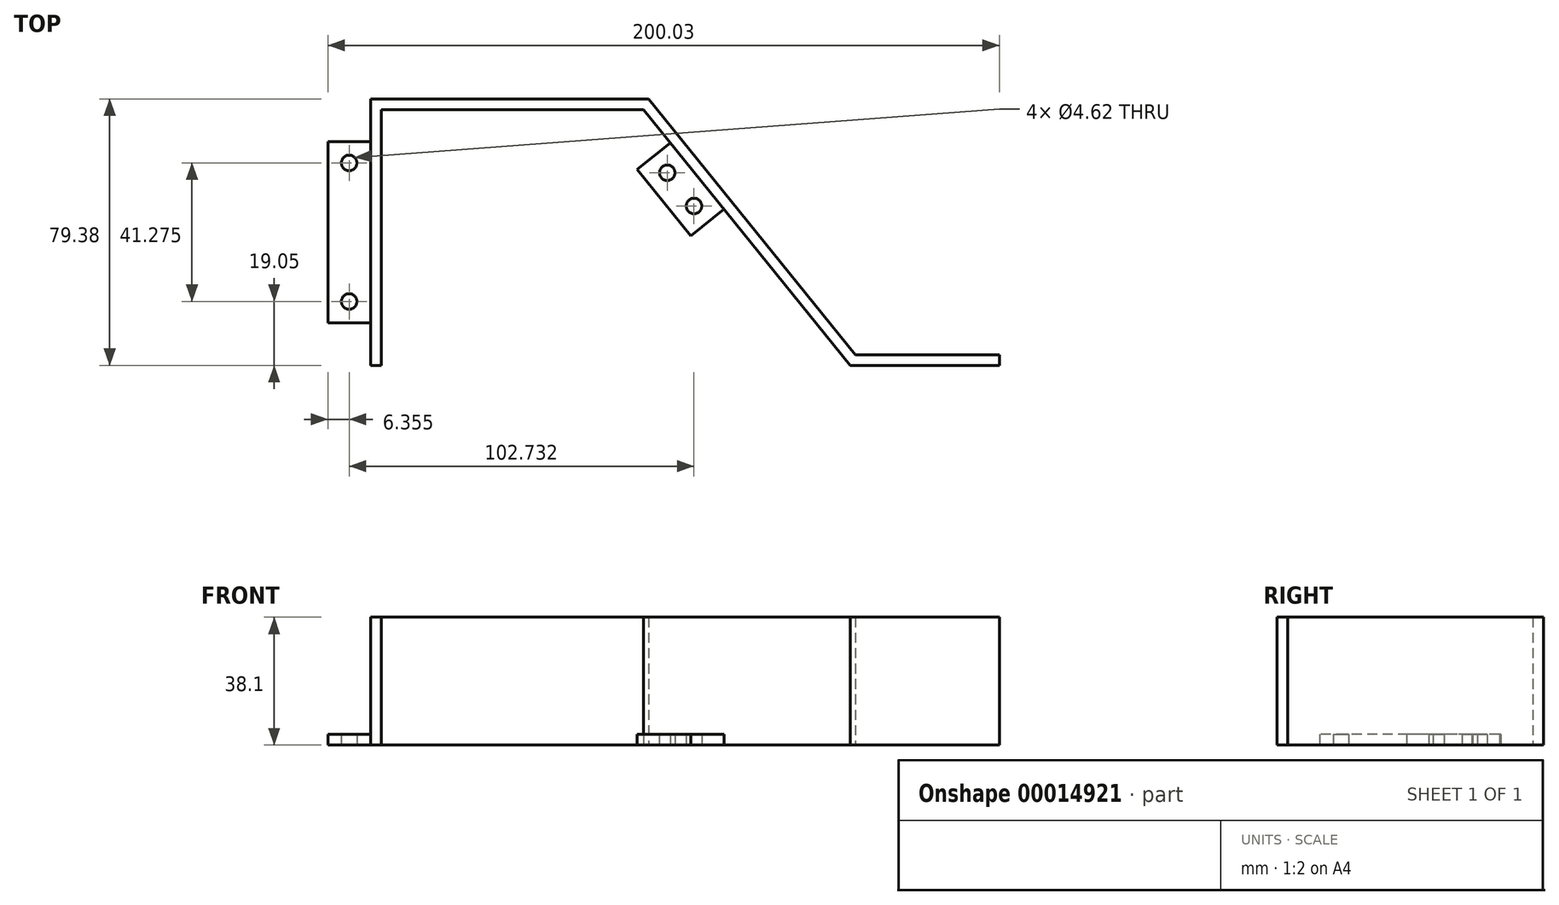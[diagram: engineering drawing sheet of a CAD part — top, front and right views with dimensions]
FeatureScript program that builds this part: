
annotation { "Feature Type Name" : "Feature", "Feature Type Description" : "" }
export const myFeature = defineFeature(function(context is Context, id is Id, definition is map)
    precondition{}
    {
        {
            var Q0;
            Q0=qCreatedBy(makeId("Top.planeOp"),FACE);
            var sketch = newSketch(context, id + "F0", { "sketchPlane" : qUnion([Q0])});
            skLineSegment(sketch, "E0", {"start": v(0, 0) * mm, "end": v(50.8, 0) * mm});
            skLineSegment(sketch, "E1", {"start": v(139.7, -76.2) * mm, "end": v(184.15, -76.2) * mm});
            skLineSegment(sketch, "E2", {"start": v(50.8, 0) * mm, "end": v(79.73, 0) * mm});
            skLineSegment(sketch, "E3", {"start": v(79.73, 0) * mm, "end": v(79.73, -24.8) * mm});
            skLineSegment(sketch, "E4", {"start": v(0, 0) * mm, "end": v(0, -76.2) * mm});
            skLineSegment(sketch, "E5.bottom", {"start": v(0, 0) * mm, "end": v(79.73, 0) * mm});
            skLineSegment(sketch, "E5.top", {"start": v(0, 3.18) * mm, "end": v(79.73, 3.18) * mm});
            skLineSegment(sketch, "E5.left", {"start": v(0, 0) * mm, "end": v(0, 3.18) * mm});
            skLineSegment(sketch, "E5.right", {"start": v(79.73, 0) * mm, "end": v(79.73, 3.17) * mm});
            skLineSegment(sketch, "E6.bottom", {"start": v(0, 3.18) * mm, "end": v(-3.18, 3.18) * mm});
            skLineSegment(sketch, "E6.top", {"start": v(0, -76.2) * mm, "end": v(-3.17, -76.2) * mm});
            skLineSegment(sketch, "E6.left", {"start": v(0, 3.18) * mm, "end": v(0, -76.2) * mm});
            skLineSegment(sketch, "E6.right", {"start": v(-3.18, 3.18) * mm, "end": v(-3.17, -76.2) * mm});
            skLineSegment(sketch, "E7.top", {"start": v(139.7, -73.02) * mm, "end": v(184.15, -73.02) * mm});
            skLineSegment(sketch, "E7.left", {"start": v(139.7, -76.2) * mm, "end": v(139.7, -73.02) * mm});
            skLineSegment(sketch, "E7.right", {"start": v(184.15, -76.2) * mm, "end": v(184.15, -73.02) * mm});
            skLineSegment(sketch, "E8", {"start": v(79.73, 0) * mm, "end": v(139.7, -76.2) * mm});
            skLineSegment(sketch, "E9.bottom", {"start": v(77.26, 1.18) * mm, "end": v(139.7, -76.2) * mm});
            skLineSegment(sketch, "E9.top", {"start": v(79.73, 3.18) * mm, "end": v(142.17, -74.2) * mm});
            skLineSegment(sketch, "E9.left", {"start": v(77.26, 1.18) * mm, "end": v(79.73, 3.17) * mm});
            skLineSegment(sketch, "E9.right", {"start": v(139.7, -76.2) * mm, "end": v(142.17, -74.2) * mm});
            skLineSegment(sketch, "E10", {"start": v(139.7, -76.2) * mm, "end": v(50.8, 0) * mm});
            skSolve(sketch);
        }
        {
            var Q0;
            {var subQ3=sQuery(id+"F0.wireOp",EDGE,"E6.bottom");Q0=makeQuery(id+"F0.imprint","IMPRINT",FACE,{"disambiguationData":[TD([[makeQuery(id+"F0.imprint","IMPRINT",EDGE,{"derivedFrom":subQ3}),1.0]])]});}
            var Q1;
            {var subQ5=sQuery(id+"F0.wireOp",EDGE,"E5.top");Q1=makeQuery(id+"F0.imprint","IMPRINT",FACE,{"disambiguationData":[TD([[makeQuery(id+"F0.imprint","IMPRINT",EDGE,{"derivedFrom":subQ5}),-1.0]])]});}
            var Q2;
            {var subQ4=sQuery(id+"F0.wireOp",EDGE,"E5.right");Q2=makeQuery(id+"F0.imprint","IMPRINT",FACE,{"disambiguationData":[TD([[makeQuery(id+"F0.imprint","IMPRINT",EDGE,{"derivedFrom":subQ4}),1.0]])]});}
            var Q3;
            {var subQ0=sQuery(id+"F0.wireOp",EDGE,"E9.bottom");var subQ3=sQuery(id+"F0.wireOp",EDGE,"E3");var subQ4=makeQuery(id+"F0.imprint","INTERSECT",VERTEX,{"derivedFrom":[subQ3,subQ0]});Q3=makeQuery(id+"F0.imprint","IMPRINT",FACE,{"disambiguationData":[TD([[makeQuery(id+"F0.imprint","IMPRINT",EDGE,{"disambiguationData":[TD([[subQ4,1.0]])],"derivedFrom":subQ0}),1.0]])]});}
            var Q4;
            {var subQ3=sQuery(id+"F0.wireOp",EDGE,"E8");Q4=makeQuery(id+"F0.imprint","IMPRINT",FACE,{"disambiguationData":[TD([[makeQuery(id+"F0.imprint","IMPRINT",EDGE,{"derivedFrom":subQ3}),-1.0]])]});}
            var Q5;
            {var subQ3=sQuery(id+"F0.wireOp",EDGE,"E5.right");Q5=makeQuery(id+"F0.imprint","IMPRINT",FACE,{"disambiguationData":[TD([[makeQuery(id+"F0.imprint","IMPRINT",EDGE,{"derivedFrom":subQ3}),-1.0]])]});}
            var Q6;
            {var subQ4=sQuery(id+"F0.wireOp",EDGE,"E7.left");Q6=makeQuery(id+"F0.imprint","IMPRINT",FACE,{"disambiguationData":[TD([[makeQuery(id+"F0.imprint","IMPRINT",EDGE,{"derivedFrom":subQ4}),-1.0]])]});}
            var Q7;
            Q7=makeQuery(id+"F0.imprint","IMPRINT",FACE,{"disambiguationData":[TD([[makeQuery(id+"F0.imprint","IMPRINT",EDGE,{"derivedFrom":sQuery(id+"F0.wireOp",EDGE,"E1")}),1.0]])]});
            extrude(context, id + "F1", {"entities" : qUnion([Q0, Q1, Q2, Q3, Q4, Q5, Q6, Q7]), "depth" : 38.1 * mm});
        }
        {
            var Q0;
            Q0=qCreatedBy(makeId("Top.planeOp"),FACE);
            var sketch = newSketch(context, id + "F2", { "sketchPlane" : qUnion([Q0])});
            skLineSegment(sketch, "E11.bottom", {"start": v(86.19, -9.88) * mm, "end": v(76.3, -17.86) * mm});
            skLineSegment(sketch, "E11.top", {"start": v(102.14, -29.65) * mm, "end": v(92.25, -37.63) * mm});
            skLineSegment(sketch, "E11.left", {"start": v(86.19, -9.88) * mm, "end": v(102.14, -29.65) * mm});
            skLineSegment(sketch, "E11.right", {"start": v(76.3, -17.86) * mm, "end": v(92.25, -37.63) * mm});
            skCircle(sketch, "E12", {"center": v(85.23, -18.81) * mm, "radius": 2.31 * mm});
            skCircle(sketch, "E13", {"center": v(93.2, -28.7) * mm, "radius": 2.31 * mm});
            skLineSegment(sketch, "E14.bottom", {"start": v(-15.88, -9.52) * mm, "end": v(-3.18, -9.52) * mm});
            skLineSegment(sketch, "E14.top", {"start": v(-15.88, -63.5) * mm, "end": v(-3.18, -63.5) * mm});
            skLineSegment(sketch, "E14.left", {"start": v(-15.88, -9.52) * mm, "end": v(-15.88, -63.5) * mm});
            skLineSegment(sketch, "E14.right", {"start": v(-3.18, -9.52) * mm, "end": v(-3.18, -63.5) * mm});
            skCircle(sketch, "E15", {"center": v(-9.53, -57.15) * mm, "radius": 2.31 * mm});
            skCircle(sketch, "E16", {"center": v(-9.53, -15.88) * mm, "radius": 2.31 * mm});
            skSolve(sketch);
        }
        {
            var Q0;
            Q0=makeQuery(id+"F2.imprint","IMPRINT",FACE,{"disambiguationData":[TD([[makeQuery(id+"F2.imprint","IMPRINT",EDGE,{"derivedFrom":sQuery(id+"F2.wireOp",EDGE,"E11.bottom")}),1.0]])]});
            var Q1;
            Q1=makeQuery(id+"F2.imprint","IMPRINT",FACE,{"disambiguationData":[TD([[makeQuery(id+"F2.imprint","IMPRINT",EDGE,{"derivedFrom":sQuery(id+"F2.wireOp",EDGE,"E14.bottom")}),-1.0]])]});
            extrude(context, id + "F3", {"entities" : qUnion([Q0, Q1]), "operationType" : NewBodyOperationType.ADD, "depth" : 3.17 * mm});
        }
    });
